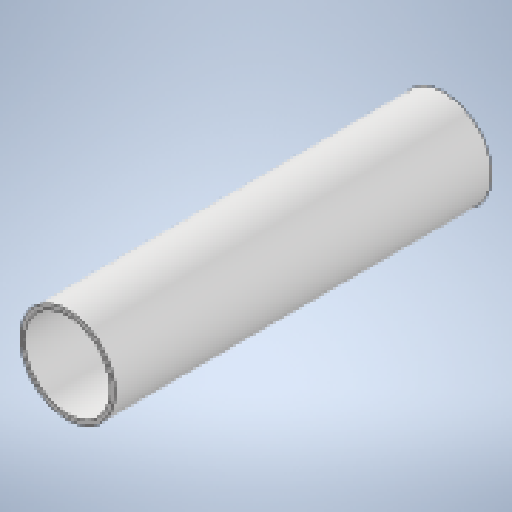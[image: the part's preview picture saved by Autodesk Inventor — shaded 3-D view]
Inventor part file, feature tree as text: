
AUTODESK INVENTOR PART (.ipt)
format: ipt  version: 2025.3 (Build 293356030, 356C)  size: 143,872 bytes
history: native  units: mm
features: extrude x1, sketch x1
ambient origin geometry x8: Origin, YZ Plane, XZ Plane, XY Plane, X Axis, Y Axis, Z Axis, Center Point
bodies: Solid1 (feature_tree)
feature tree (2):
  extrude  "Extrusion1"  Depth=250.0mm
  sketch  "Sketch1"  dims[d0=57.0mm d1=3.0mm d2=250.0mm d3=0.0mm]
